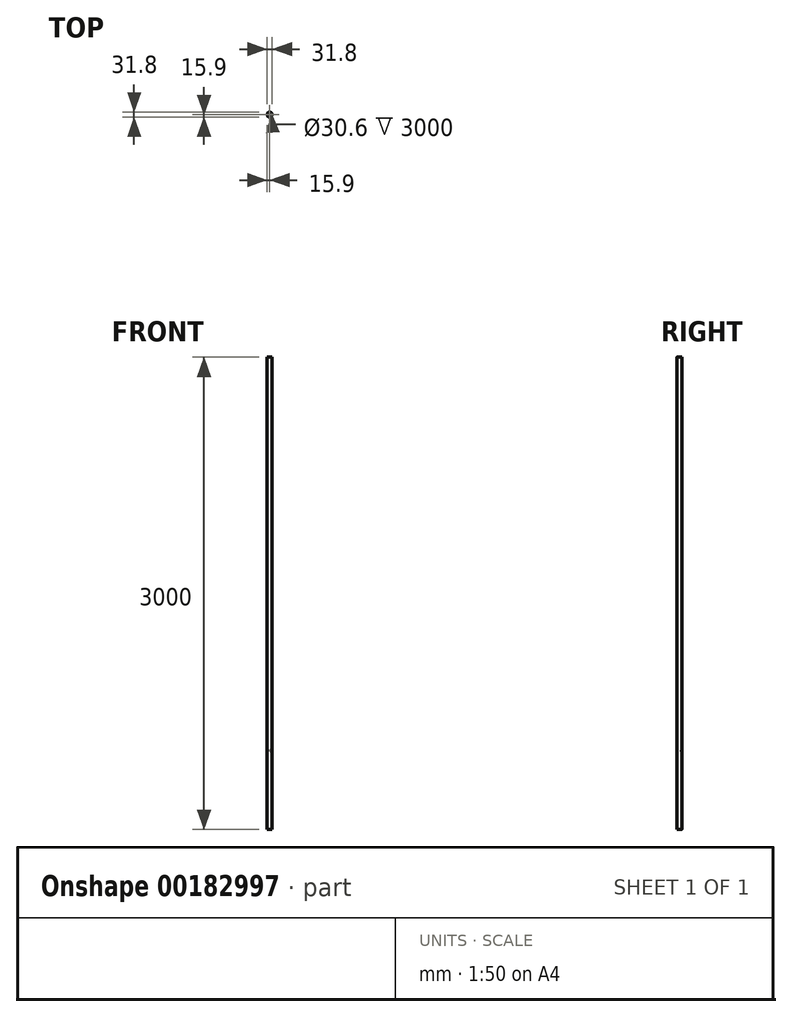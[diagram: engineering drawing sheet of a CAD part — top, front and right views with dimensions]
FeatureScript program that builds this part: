
annotation { "Feature Type Name" : "Feature", "Feature Type Description" : "" }
export const myFeature = defineFeature(function(context is Context, id is Id, definition is map)
    precondition{}
    {
        {
            var Q0;
            Q0=qCreatedBy(makeId("Top.planeOp"),FACE);
            var sketch = newSketch(context, id + "F0", { "sketchPlane" : qUnion([Q0])});
            skCircle(sketch, "E0", {"center": v(0, 0) * mm, "radius": 15.9 * mm});
            skCircle(sketch, "E1", {"center": v(0, 0) * mm, "radius": 15.3 * mm});
            skSolve(sketch);
        }
        {
            var Q0;
            Q0 = qSketchRegion(id + "F0", true);
            extrude(context, id + "F1", {"entities" : qUnion([Q0]), "depth" : 3000 * mm});
        }
        {
            var Q0;
            Q0=qCreatedBy(makeId("Front.planeOp"),FACE);
            var sketch = newSketch(context, id + "F2", { "sketchPlane" : qUnion([Q0])});
            skCircle(sketch, "E2", {"center": v(0, 500) * mm, "radius": 6 * mm});
            skSolve(sketch);
        }
        {
            var Q0;
            Q0 = qSketchRegion(id + "F2", true);
            extrude(context, id + "F3", {"entities" : qUnion([Q0]), "operationType" : NewBodyOperationType.REMOVE, "oppositeDirection" : true, "depth" : 15 * mm});
        }
    });
